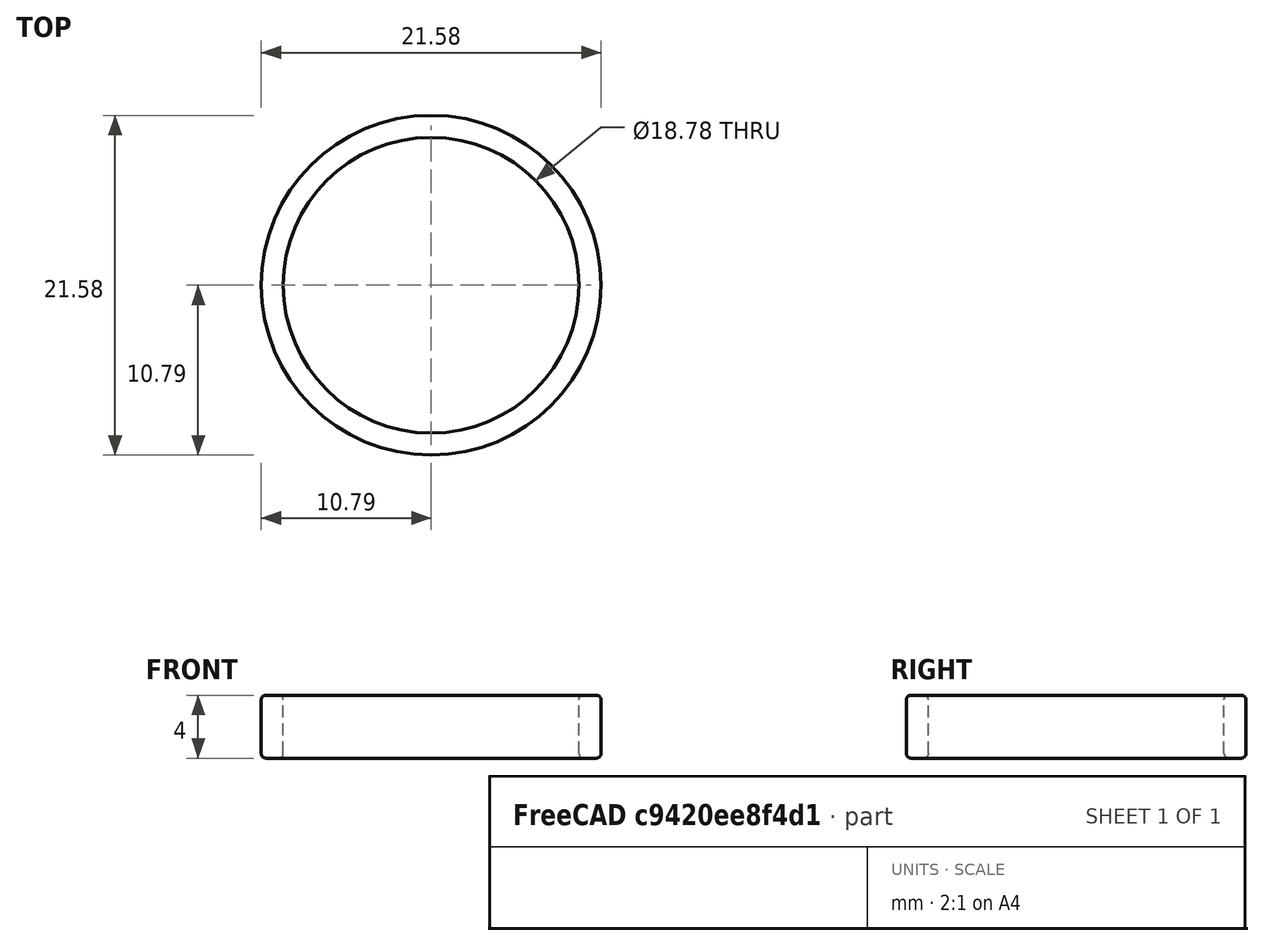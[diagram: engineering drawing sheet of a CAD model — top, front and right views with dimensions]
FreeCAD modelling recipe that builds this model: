
FCSTD DOCUMENT  (FreeCAD 0.21R33771 (Git))
Label: wedding_ring_circumference_P14
License: All rights reserved
LicenseURL: http://en.wikipedia.org/wiki/All_rights_reserved
objects: Spreadsheet::Sheet×1, Sketcher::SketchObject×1, PartDesign::Revolution×1, PartDesign::Body×1
note: 4 computed .brp shape members not serialized (recipe doc carries the construction recipe); baked Part::Feature solids carry a one-line shape summary decoded from their .brp

FEATURE [Spreadsheet::Sheet] Spreadsheet  label="settings"
  cells = A1='ring Width; B1(ring_width)=4; C1='Edge fillet size; D1(ring_edge_fillet)=0.3; A2='ring circumference; B2(ring_circumference)=59; A3='ring thickness; B3(ring_thickness)=1.4; A5='Calculations; A6='Center revolve distance; B6(calc_revolve_distance)==ring_circumference / (2 * pi); A7='Center outer distance; B7(calc_outer_revolve_distance)==calc_revolve_distance + ring_thickness
FEATURE [Sketcher::SketchObject] Sketch
  FullyConstrained = true
  MapMode = 5
  Placement = pos=(0,0,0) rot=(1,0,0;1.5708rad)
  Support = -> [XZ_Plane]
  expr: Constraints[12] = <<settings>>.ring_thickness
  expr: Constraints[15] = <<settings>>.ring_edge_fillet
  expr: Constraints[20] = <<settings>>.ring_edge_fillet
  expr: Constraints[38] = <<settings>>.ring_edge_fillet
  expr: Constraints[39] = <<settings>>.ring_edge_fillet
  expr: Constraints[8] = <<settings>>.calc_outer_revolve_distance
  expr: Constraints[9] = <<settings>>.ring_width
  sketch-geometry (13):
    g0: LineSegment StartX=0 StartY=0 StartZ=0 EndX=-10.7901 EndY=0 EndZ=0
    g1: LineSegment StartX=-10.7901 StartY=0 StartZ=0 EndX=-10.7901 EndY=4 EndZ=0
    g2: LineSegment StartX=-10.7901 StartY=4 StartZ=0 EndX=0 EndY=4 EndZ=0
    g3: LineSegment StartX=0 StartY=4 StartZ=0 EndX=0 EndY=0 EndZ=0
    g4: LineSegment StartX=-9.39014 StartY=4 StartZ=0 EndX=-9.39014 EndY=0 EndZ=0
    g5: ArcOfCircle CenterX=-10.4901 CenterY=0.3 CenterZ=0 NormalX=0 NormalY=0 NormalZ=1 AngleXU=0 Radius=0.3 StartAngle=3.14159 EndAngle=4.71239
    g6: ArcOfCircle CenterX=-9.69014 CenterY=0.3 CenterZ=0 NormalX=0 NormalY=0 NormalZ=1 AngleXU=0 Radius=0.3 StartAngle=4.71239 EndAngle=6.28319
    g7: LineSegment StartX=-10.4901 StartY=0 StartZ=0 EndX=-9.69014 EndY=0 EndZ=0
    g8: ArcOfCircle CenterX=-10.4901 CenterY=3.7 CenterZ=0 NormalX=0 NormalY=0 NormalZ=1 AngleXU=0 Radius=0.3 StartAngle=1.5708 EndAngle=3.14159
    g9: ArcOfCircle CenterX=-9.69014 CenterY=3.7 CenterZ=0 NormalX=0 NormalY=0 NormalZ=1 AngleXU=0 Radius=0.3 StartAngle=6e-16 EndAngle=1.5708
    g10: LineSegment StartX=-10.7901 StartY=3.7 StartZ=0 EndX=-10.7901 EndY=0.3 EndZ=0
    g11: LineSegment StartX=-9.39014 StartY=0.3 StartZ=0 EndX=-9.39014 EndY=3.7 EndZ=0
    g12: LineSegment StartX=-9.69014 StartY=4 StartZ=0 EndX=-10.4901 EndY=4 EndZ=0
  constraints (43):
    c: Coincident(g0,g1)
    c: Coincident(g1,g2)
    c: Coincident(g2,g3)
    c: Coincident(g3,g0)
    c: Horizontal(g0)
    c: Horizontal(g2)
    c: Vertical(g3)
    c: Coincident(g0,g-1)
    c: Distance(g0,g0) = 10.7901
    c: Distance(g1,g0) = 4
    c: PointOnObject(g4,g2)
    c: PointOnObject(g4,g0)
    c: Distance(g1,g4) = 1.4
    c: PointOnObject(g5,g1)
    c: PointOnObject(g5,g0)
    c: Distance(g5,g0) = 0.3
    c: Vertical(g5,g5)
    c: Horizontal(g5,g5)
    c: PointOnObject(g6,g4)
    c: PointOnObject(g6,g0)
    c: Distance(g6,g4) = 0.3
    c: Vertical(g6,g6)
    c: Horizontal(g6,g6)
    c: Coincident(g7,g6)
    c: PointOnObject(g8,g2)
    c: PointOnObject(g8,g1)
    c: PointOnObject(g9,g2)
    c: PointOnObject(g9,g4)
    c: Vertical(g8,g8)
    c: Horizontal(g8,g8)
    c: Vertical(g9,g9)
    c: Horizontal(g9,g9)
    c: Coincident(g10,g5)
    c: Vertical(g10)
    c: Coincident(g11,g6)
    c: Coincident(g11,g9)
    c: Coincident(g12,g9)
    c: Coincident(g12,g8)
    c: Distance(g1,g8) = 0.3
    c: Distance(g9,g4) = 0.3
    c: Vertical(g4)
    c: Coincident(g10,g8)
    c: Coincident(g7,g5)
FEATURE [PartDesign::Revolution] Revolution
  Angle = 360
  Axis = (0,-2e-16,1)
  Base = (0,0,0)
  Placement = pos=(0,0,0) rot=(1,0,0;1.5708rad)
  Profile = -> Sketch
  ReferenceAxis = -> Sketch [V_Axis]
FEATURE [PartDesign::Body] Body
  Group = -> [Sketch,Revolution]
  Origin = -> Origin
  Tip = -> Revolution
